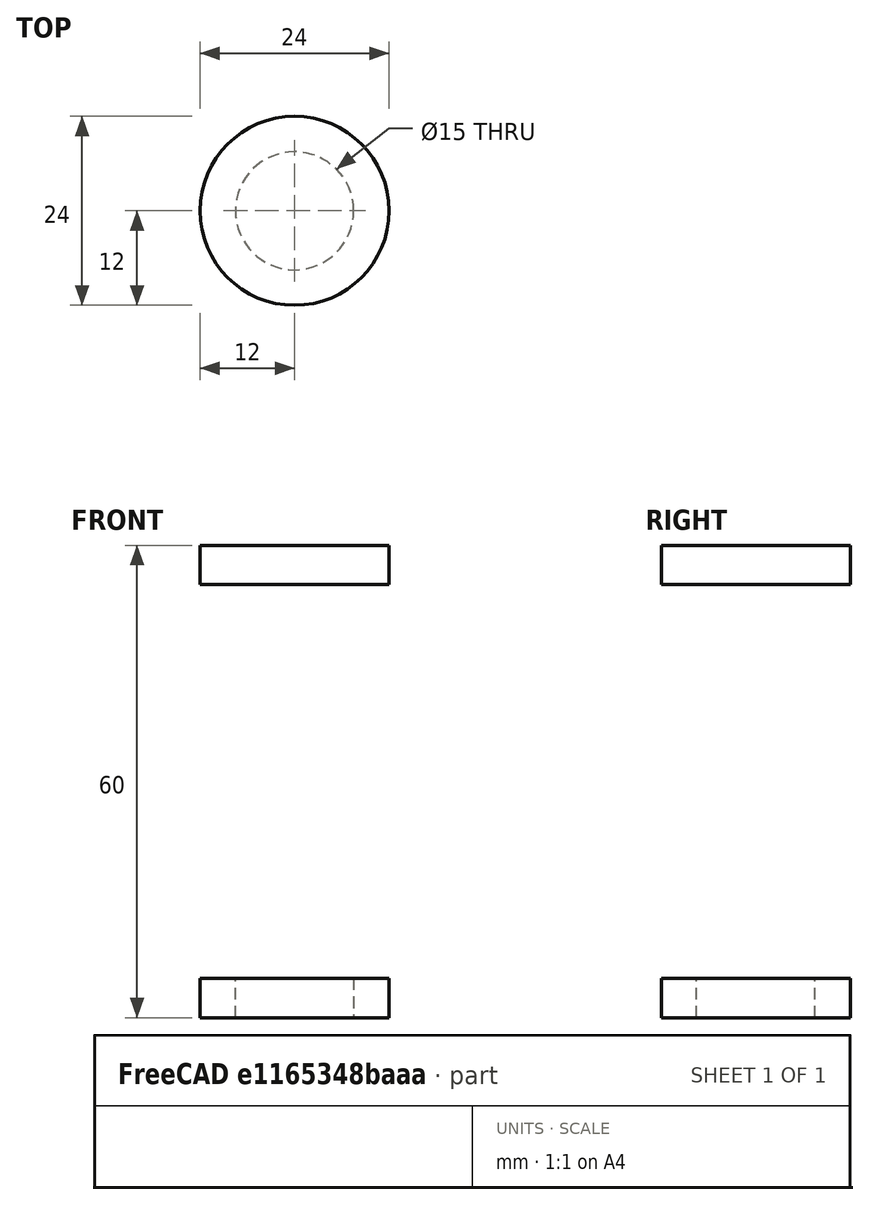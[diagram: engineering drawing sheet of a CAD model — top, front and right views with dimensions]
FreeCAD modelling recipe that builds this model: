
FCSTD DOCUMENT  (FreeCAD 0.16R6700 (Git))
Label: string_drive
License: All rights reserved
LicenseURL: http://en.wikipedia.org/wiki/All_rights_reserved
objects: Mesh::Feature×1, Part::Cylinder×1, Sketcher::SketchObject×1, PartDesign::Pocket×1, Part::FeaturePython×1
note: 5 computed .brp shape members not serialized (recipe doc carries the construction recipe); baked Part::Feature solids carry a one-line shape summary decoded from their .brp

FEATURE [Mesh::Feature] string_guide_full
FEATURE [Part::Cylinder] Cylinder
  Angle = 360
  Height = 5
  Placement = pos=(0,0,5) rot=(0,0,1;0rad)
  Radius = 12
FEATURE [Sketcher::SketchObject] Sketch
  Placement = pos=(0,0,10) rot=(0,0,1;0rad)
  Support = -> Cylinder [Face2]
  sketch-geometry (1):
    g0: Circle CenterX=0 CenterY=0 CenterZ=0 NormalX=0 NormalY=0 NormalZ=1 Radius=7.5
  constraints (2):
    c: Coincident(g0,g-1)
    c: Radius(g0) = 7.5
FEATURE [PartDesign::Pocket] Pocket  label="bearing 6802"
  Length = 5
  Placement = pos=(0,0,5) rot=(0,0,1;0rad)
  Sketch = -> Sketch
  Type = 0
FEATURE [Part::FeaturePython] Clone  label="Clone of bearing 6802"  # Draft clone (typed FeaturePython)
  Objects = -> [Pocket]
  Placement = pos=(0,0,-50) rot=(0,0,1;0rad)
  Scale = (1,1,1)
